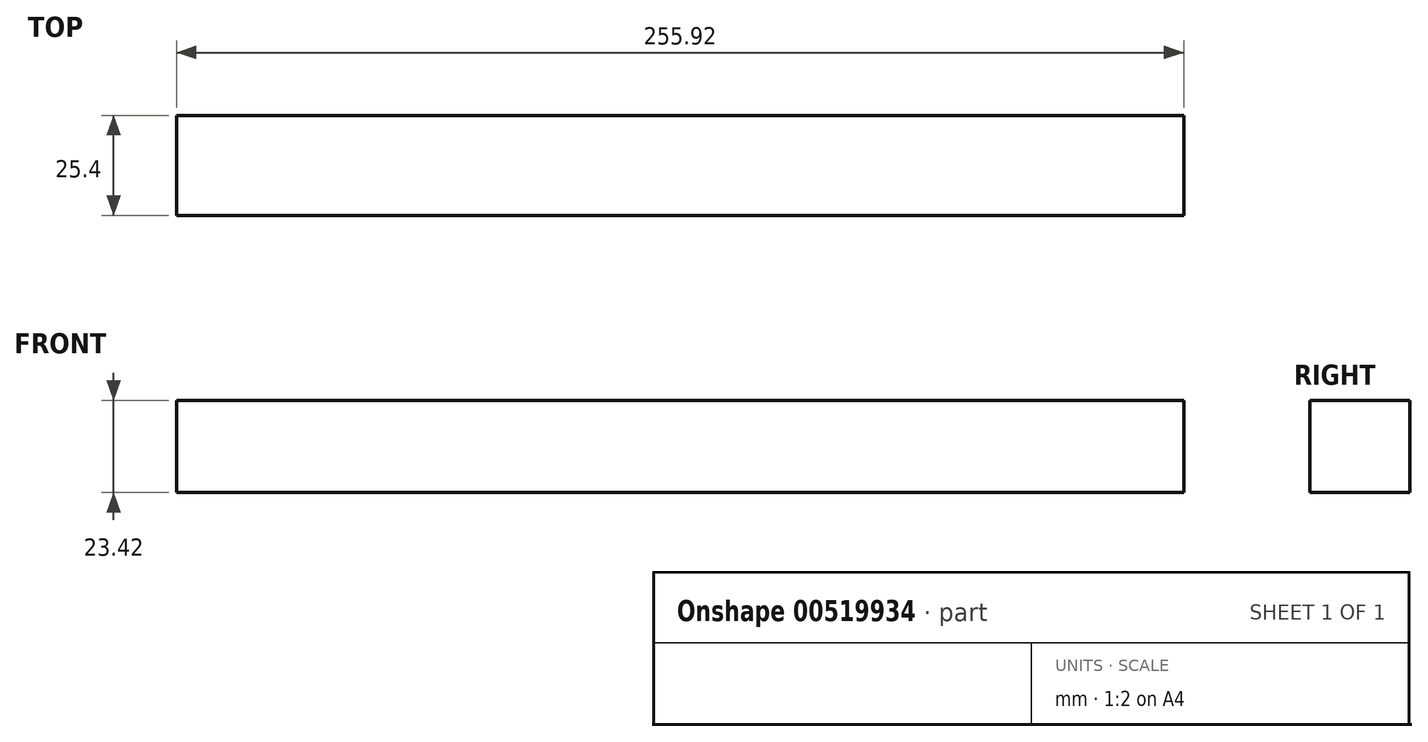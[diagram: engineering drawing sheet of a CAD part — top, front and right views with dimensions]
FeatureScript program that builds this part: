
annotation { "Feature Type Name" : "Feature", "Feature Type Description" : "" }
export const myFeature = defineFeature(function(context is Context, id is Id, definition is map)
    precondition{}
    {
        {
            var Q0;
            Q0=qCreatedBy(makeId("Front.planeOp"),FACE);
            var sketch = newSketch(context, id + "F0", { "sketchPlane" : qUnion([Q0])});
            skLineSegment(sketch, "E0.bottom", {"start": v(127.96, -11.7) * mm, "end": v(-127.96, -11.7) * mm});
            skLineSegment(sketch, "E0.top", {"start": v(127.96, 11.7) * mm, "end": v(-127.96, 11.7) * mm});
            skLineSegment(sketch, "E0.left", {"start": v(127.96, -11.7) * mm, "end": v(127.96, 11.7) * mm});
            skLineSegment(sketch, "E0.right", {"start": v(-127.96, -11.7) * mm, "end": v(-127.96, 11.7) * mm});
            skPoint(sketch, "E0.middle", {"position": v(0, 0) * mm});
            skSolve(sketch);
        }
        {
            var Q0;
            Q0=qCreatedBy(makeId("Front.planeOp"),FACE);
            var sketch = newSketch(context, id + "F1", { "sketchPlane" : qUnion([Q0])});
            skSolve(sketch);
        }
        {
            var Q0;
            Q0 = qSketchRegion(id + "F1", true);
            var Q1;
            Q1=makeQuery(id+"F0.imprint","IMPRINT",FACE,{"disambiguationData":[TD([[makeQuery(id+"F0.imprint","IMPRINT",EDGE,{"derivedFrom":sQuery(id+"F0.wireOp",EDGE,"E0.bottom")}),-1.0]])]});
            extrude(context, id + "F2", {"entities" : qUnion([Q0, Q1]), "depth" : 25.4 * mm, "offsetDistance" : 25.4 * mm});
        }
    });
